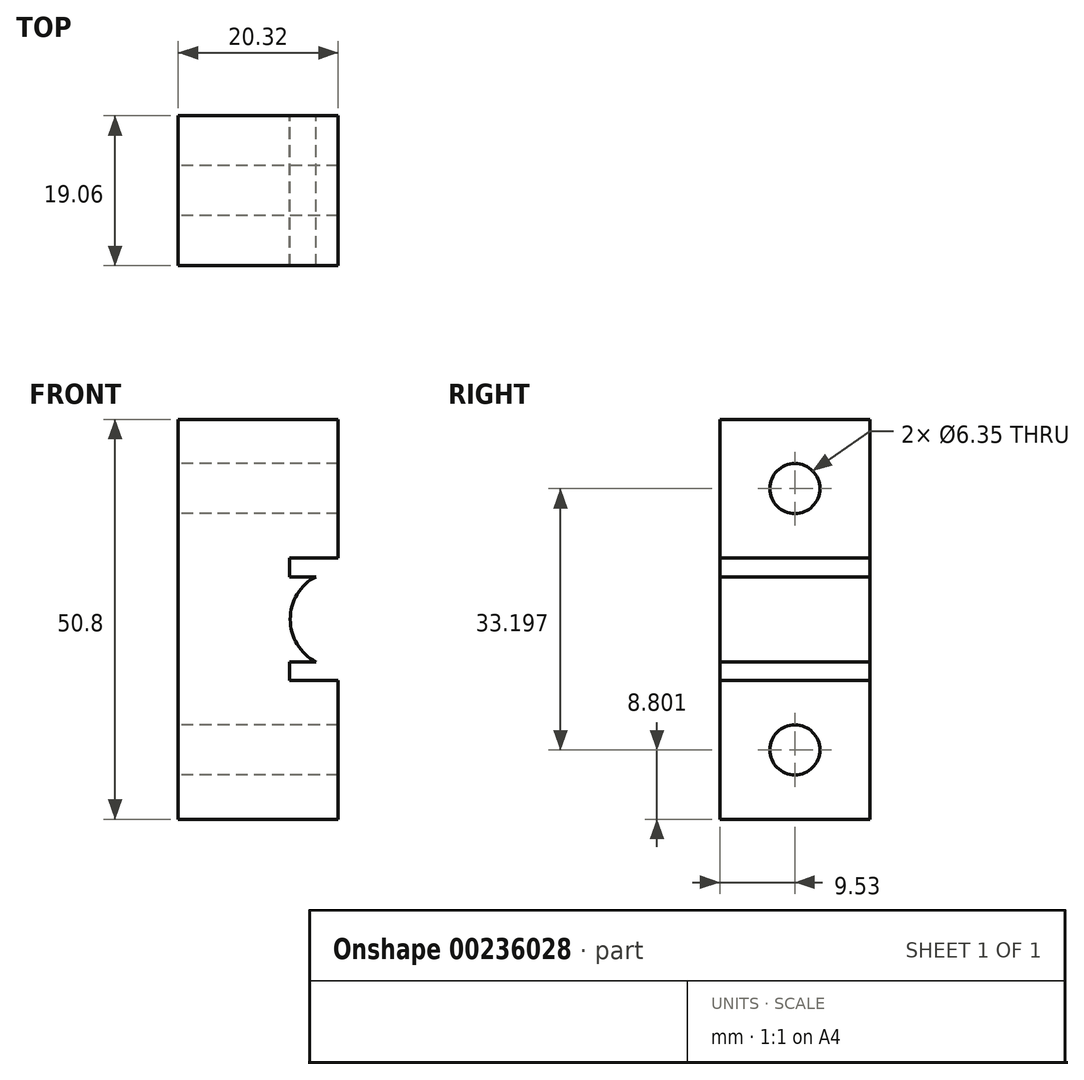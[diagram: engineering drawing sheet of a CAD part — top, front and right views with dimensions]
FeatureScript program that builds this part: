
annotation { "Feature Type Name" : "Feature", "Feature Type Description" : "" }
export const myFeature = defineFeature(function(context is Context, id is Id, definition is map)
    precondition{}
    {
        {
            var Q0;
            Q0=qCreatedBy(makeId("Front.planeOp"),FACE);
            var sketch = newSketch(context, id + "F0", { "sketchPlane" : qUnion([Q0])});
            skLineSegment(sketch, "E0.bottom", {"start": v(-10.16, 25.4) * mm, "end": v(10.16, 25.4) * mm, "construction": true});
            skLineSegment(sketch, "E0.top", {"start": v(-10.16, -25.4) * mm, "end": v(10.16, -25.4) * mm, "construction": true});
            skLineSegment(sketch, "E0.left", {"start": v(-10.16, 25.4) * mm, "end": v(-10.16, -25.4) * mm, "construction": true});
            skLineSegment(sketch, "E0.right", {"start": v(10.16, 25.4) * mm, "end": v(10.16, -25.4) * mm, "construction": true});
            skPoint(sketch, "E0.middle", {"position": v(0, 0) * mm});
            skLineSegment(sketch, "E1.bottom", {"start": v(4, 7.8) * mm, "end": v(8.4, 7.8) * mm, "construction": true});
            skLineSegment(sketch, "E1.left", {"start": v(4, 7.8) * mm, "end": v(4, 5.4) * mm, "construction": true});
            skPoint(sketch, "E1.middle", {"position": v(6.2, 6.6) * mm});
            skLineSegment(sketch, "E2.MirrorCS", {"start": v(4, -7.8) * mm, "end": v(4, -5.4) * mm, "construction": true});
            skLineSegment(sketch, "E3.MirrorCS", {"start": v(4, -7.8) * mm, "end": v(8.4, -7.8) * mm, "construction": true});
            skLineSegment(sketch, "E4", {"start": v(4, 7.8) * mm, "end": v(10.16, 7.8) * mm});
            skLineSegment(sketch, "E5", {"start": v(10.16, 25.4) * mm, "end": v(10.16, 7.8) * mm});
            skLineSegment(sketch, "E6", {"start": v(10.16, 25.4) * mm, "end": v(-10.16, 25.4) * mm});
            skLineSegment(sketch, "E7", {"start": v(-10.16, 25.4) * mm, "end": v(-10.16, -25.4) * mm});
            skLineSegment(sketch, "E8", {"start": v(-10.16, -25.4) * mm, "end": v(10.16, -25.4) * mm});
            skArc(sketch, "E9", {"start": v(7.34, 5.4) * mm, "mid": v(4.07, 0) * mm, "end": v(7.33, -5.4) * mm});
            skLineSegment(sketch, "E10", {"start": v(4, 7.8) * mm, "end": v(4, 5.4) * mm});
            skLineSegment(sketch, "E11", {"start": v(4, 5.4) * mm, "end": v(7.34, 5.4) * mm});
            skLineSegment(sketch, "E12", {"start": v(4, -5.4) * mm, "end": v(7.33, -5.4) * mm});
            skLineSegment(sketch, "E13", {"start": v(4, -5.4) * mm, "end": v(4, -7.8) * mm});
            skLineSegment(sketch, "E14", {"start": v(4, -7.8) * mm, "end": v(10.16, -7.8) * mm});
            skLineSegment(sketch, "E15", {"start": v(10.16, -7.8) * mm, "end": v(10.16, -25.4) * mm});
            skSolve(sketch);
        }
        {
            var Q0;
            Q0=makeQuery(id+"F0.imprint","IMPRINT",FACE,{"disambiguationData":[TD([[makeQuery(id+"F0.imprint","IMPRINT",EDGE,{"derivedFrom":sQuery(id+"F0.wireOp",EDGE,"E4")}),1.0]])]});
            extrude(context, id + "F1", {"entities" : qUnion([Q0]), "endBound" : BoundingType.SYMMETRIC, "depth" : 19.05 * mm});
        }
        {
            var Q0;
            Q0=makeQuery(id+"F1.opExtrude","SWEPT_FACE",FACE,{"disambiguationData":[OSD([sQuery(id+"F0.wireOp",EDGE,"E7")])]});
            var sketch = newSketch(context, id + "F2", { "sketchPlane" : qUnion([Q0])});
            skPoint(sketch, "E16", {"position": v(0, 16.6) * mm});
            skPoint(sketch, "E17", {"position": v(0, -16.6) * mm});
            skLineSegment(sketch, "E18.0", {"start": v(9.53, 7.8) * mm, "end": v(-9.52, 7.8) * mm});
            skLineSegment(sketch, "E19.0", {"start": v(9.53, 25.4) * mm, "end": v(-9.52, 25.4) * mm});
            skLineSegment(sketch, "E20.0", {"start": v(9.53, -25.4) * mm, "end": v(-9.52, -25.4) * mm});
            skLineSegment(sketch, "E21.0", {"start": v(9.53, -7.8) * mm, "end": v(-9.52, -7.8) * mm});
            skLineSegment(sketch, "E22", {"start": v(0, 7.8) * mm, "end": v(0, 25.4) * mm, "construction": true});
            skLineSegment(sketch, "E23", {"start": v(0, -25.4) * mm, "end": v(0, -7.8) * mm, "construction": true});
            skCircle(sketch, "E24", {"center": v(0, 16.6) * mm, "radius": 3.18 * mm});
            skCircle(sketch, "E25.MirrorC", {"center": v(0, -16.6) * mm, "radius": 3.18 * mm});
            skSolve(sketch);
        }
        {
            var Q0;
            Q0=qSketchRegion(id+"F2",true);
            extrude(context, id + "F3", {"entities" : qUnion([Q0]), "operationType" : NewBodyOperationType.REMOVE, "oppositeDirection" : true, "depth" : 25.4 * mm});
        }
    });
